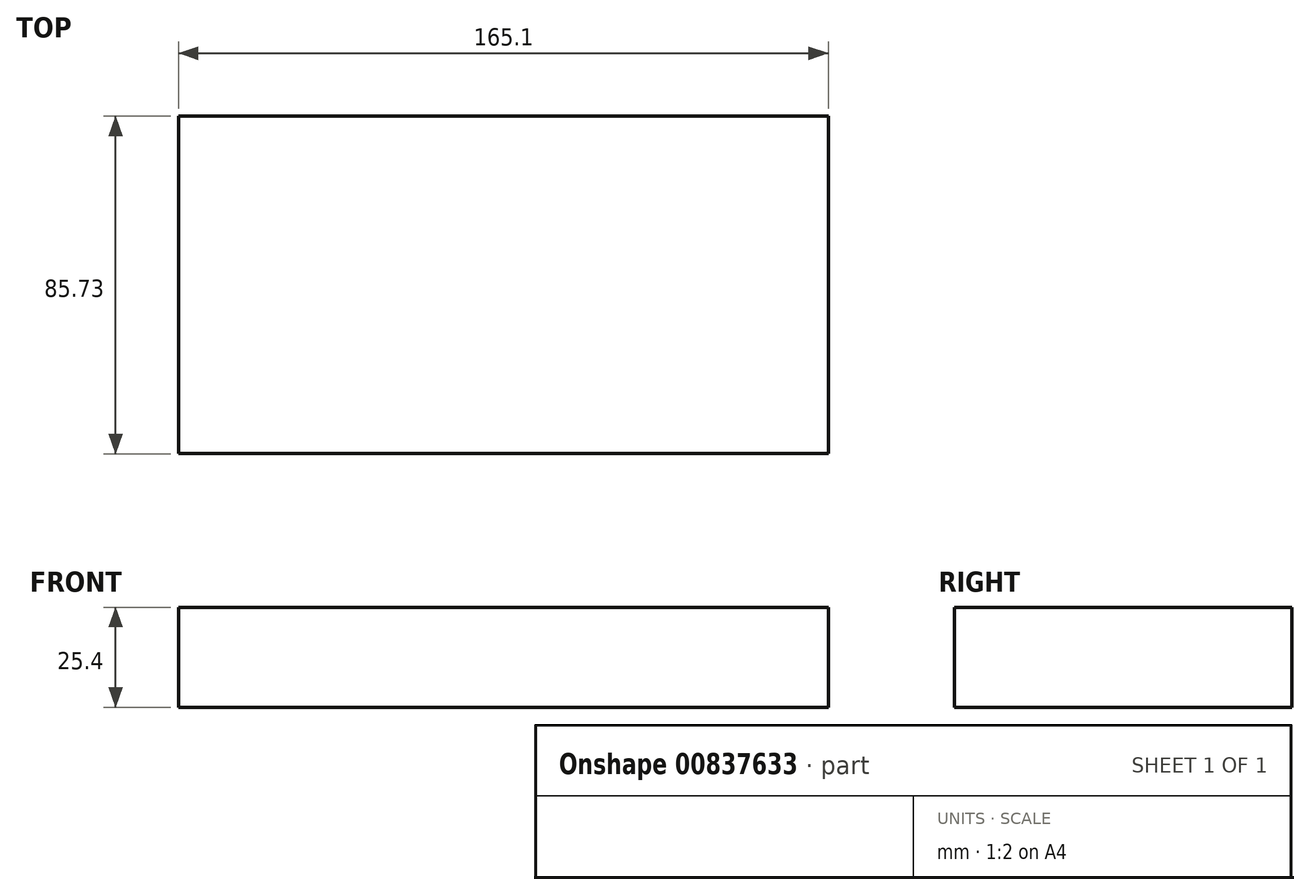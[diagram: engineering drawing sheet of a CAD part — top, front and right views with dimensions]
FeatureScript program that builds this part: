
annotation { "Feature Type Name" : "Feature", "Feature Type Description" : "" }
export const myFeature = defineFeature(function(context is Context, id is Id, definition is map)
    precondition{}
    {
        {
            var Q0;
            Q0=qCreatedBy(makeId("Top.planeOp"),FACE);
            var sketch = newSketch(context, id + "F0", { "sketchPlane" : qUnion([Q0])});
            skLineSegment(sketch, "E0.bottom", {"start": v(-183.88, 97.63) * mm, "end": v(-18.78, 97.63) * mm});
            skLineSegment(sketch, "E0.top", {"start": v(-183.88, 11.9) * mm, "end": v(-18.78, 11.9) * mm});
            skLineSegment(sketch, "E0.left", {"start": v(-183.88, 97.63) * mm, "end": v(-183.88, 11.9) * mm});
            skLineSegment(sketch, "E0.right", {"start": v(-18.78, 97.63) * mm, "end": v(-18.78, 11.9) * mm});
            skSolve(sketch);
        }
        {
            var Q0;
            Q0=makeQuery(id+"F0.imprint","IMPRINT",FACE,{"disambiguationData":[TD([[makeQuery(id+"F0.imprint","IMPRINT",EDGE,{"derivedFrom":sQuery(id+"F0.wireOp",EDGE,"E0.bottom")}),-1.0]])]});
            extrude(context, id + "F1", {"entities" : qUnion([Q0]), "depth" : 25.4 * mm, "offsetDistance" : 25.4 * mm});
        }
    });
